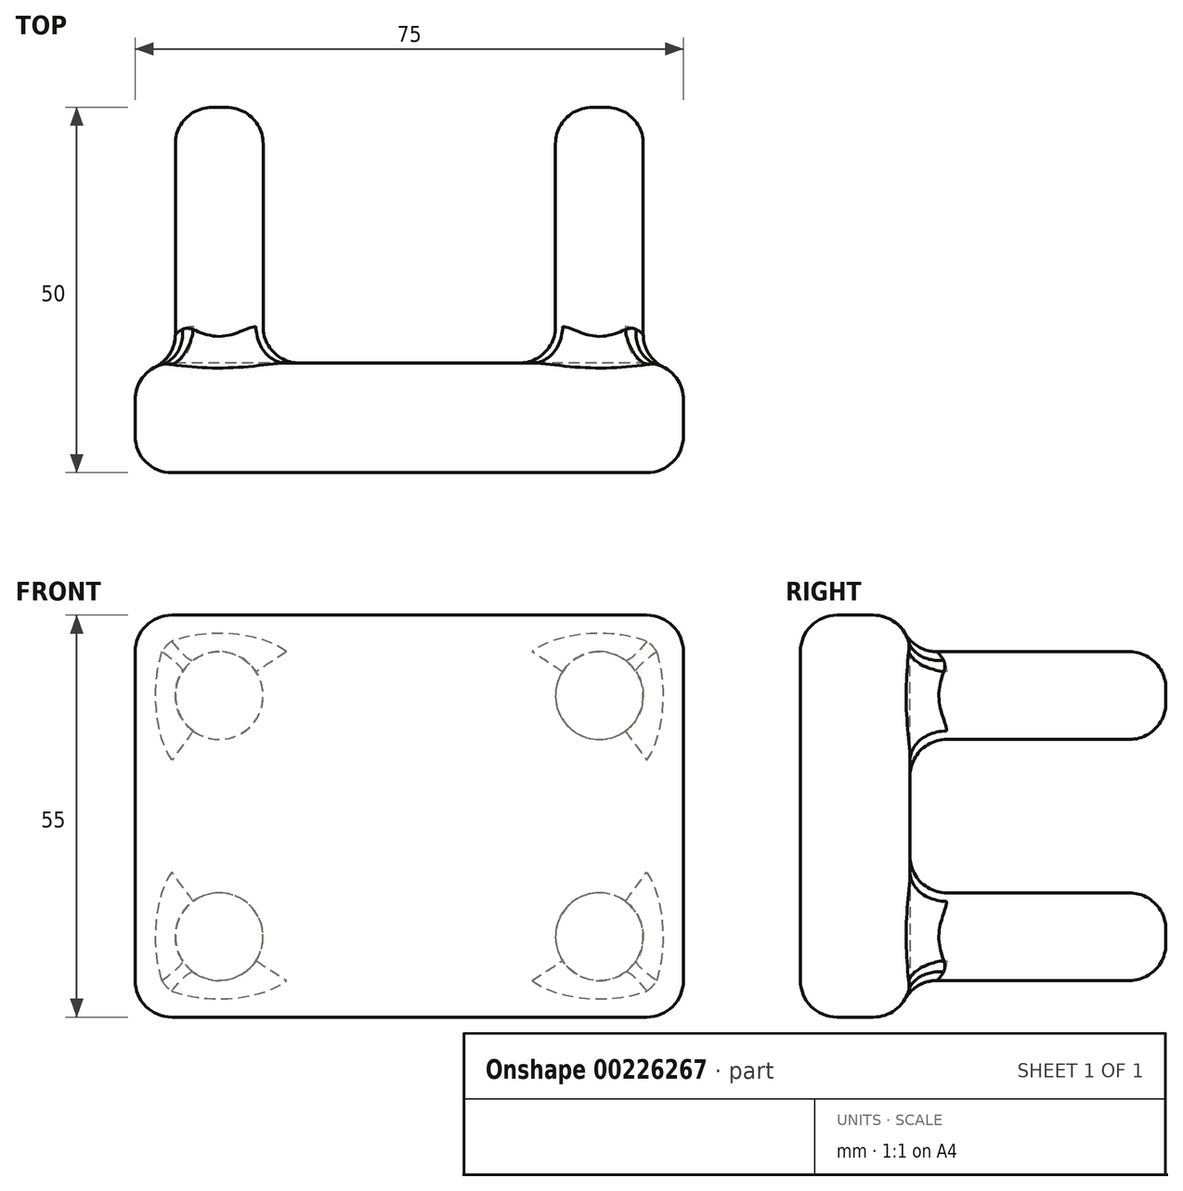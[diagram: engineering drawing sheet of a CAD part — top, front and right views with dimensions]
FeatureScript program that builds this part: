
annotation { "Feature Type Name" : "Feature", "Feature Type Description" : "" }
export const myFeature = defineFeature(function(context is Context, id is Id, definition is map)
    precondition{}
    {
        {
            var Q0;
            Q0=qCreatedBy(makeId("Front.planeOp"),FACE);
            var sketch = newSketch(context, id + "F0", { "sketchPlane" : qUnion([Q0])});
            skLineSegment(sketch, "E0.bottom", {"start": v(37.5, -27.5) * mm, "end": v(-37.5, -27.5) * mm});
            skLineSegment(sketch, "E0.top", {"start": v(37.5, 27.5) * mm, "end": v(-37.5, 27.5) * mm});
            skLineSegment(sketch, "E0.left", {"start": v(37.5, -27.5) * mm, "end": v(37.5, 27.5) * mm});
            skLineSegment(sketch, "E0.right", {"start": v(-37.5, -27.5) * mm, "end": v(-37.5, 27.5) * mm});
            skPoint(sketch, "E0.middle", {"position": v(0, 0) * mm});
            skSolve(sketch);
        }
        {
            var Q0;
            Q0 = qSketchRegion(id + "F0", true);
            extrude(context, id + "F1", {"entities" : qUnion([Q0]), "depth" : 15 * mm});
        }
        {
            var Q0;
            Q0=makeQuery(id+"F1.opExtrude","CAP_FACE",FACE,{"disambiguationData":[OSD([sQuery(id+"F0.wireOp",EDGE,"E0.bottom"),sQuery(id+"F0.wireOp",EDGE,"E0.top"),sQuery(id+"F0.wireOp",EDGE,"E0.left"),sQuery(id+"F0.wireOp",EDGE,"E0.right")])],"isStart":true});
            var sketch = newSketch(context, id + "F2", { "sketchPlane" : qUnion([Q0])});
            skCircle(sketch, "E1", {"center": v(-26, 16.5) * mm, "radius": 6 * mm});
            skCircle(sketch, "E2.MirrorC", {"center": v(26, 16.5) * mm, "radius": 6 * mm});
            skCircle(sketch, "E3.MirrorC", {"center": v(26, -16.5) * mm, "radius": 6 * mm});
            skCircle(sketch, "E4.MirrorC", {"center": v(-26, -16.5) * mm, "radius": 6 * mm});
            skSolve(sketch);
        }
        {
            var Q0;
            Q0 = qSketchRegion(id + "F2", true);
            extrude(context, id + "F3", {"entities" : qUnion([Q0]), "operationType" : NewBodyOperationType.ADD, "depth" : 35 * mm});
        }
        {
            var Q0;
            Q0=makeQuery(id+"F1.opExtrude","SWEPT_FACE",FACE,{"disambiguationData":[OSD([sQuery(id+"F0.wireOp",EDGE,"E0.top")])]});
            var Q1;
            Q1=makeQuery(id+"F1.opExtrude","CAP_FACE",FACE,{"disambiguationData":[OSD([sQuery(id+"F0.wireOp",EDGE,"E0.bottom"),sQuery(id+"F0.wireOp",EDGE,"E0.top"),sQuery(id+"F0.wireOp",EDGE,"E0.left"),sQuery(id+"F0.wireOp",EDGE,"E0.right")])],"isStart":false});
            var Q2;
            Q2=makeQuery(id+"F1.opExtrude","SWEPT_FACE",FACE,{"disambiguationData":[OSD([sQuery(id+"F0.wireOp",EDGE,"E0.right")])]});
            var Q3;
            Q3=makeQuery(id+"F1.opExtrude","SWEPT_FACE",FACE,{"disambiguationData":[OSD([sQuery(id+"F0.wireOp",EDGE,"E0.bottom")])]});
            var Q4;
            Q4=makeQuery(id+"F1.opExtrude","SWEPT_FACE",FACE,{"disambiguationData":[OSD([sQuery(id+"F0.wireOp",EDGE,"E0.left")])]});
            fillet(context, id + "F4", {"entities" : qUnion([Q0, Q1, Q2, Q3, Q4]), "radius" : 5 * mm, "tangentPropagation" : true, "allowEdgeOverflow" : false});
        }
        {
            var Q0;
            {var subQ0=sQuery(id+"F0.wireOp",EDGE,"E0.right");var subQ1=sQuery(id+"F0.wireOp",EDGE,"E0.bottom");Q0=makeQuery(id+"F4.opFillet","BLEND_FACE",FACE,{"disambiguationData":[OSD([subQ1,subQ0]),TDD([makeQuery(id+"F1.opExtrude","CAP_VERTEX",VERTEX,{"disambiguationData":[OSD([subQ1,subQ0])],"isStart":true})])]});}
            var Q1;
            {var subQ0=sQuery(id+"F0.wireOp",EDGE,"E0.right");Q1=makeQuery(id+"F4.opFillet","BLEND_FACE",FACE,{"disambiguationData":[OSD([subQ0]),TDD([makeQuery(id+"F1.opExtrude","CAP_EDGE",EDGE,{"disambiguationData":[OSD([subQ0])],"isStart":true})])]});}
            var Q2;
            {var subQ0=sQuery(id+"F0.wireOp",EDGE,"E0.right");Q2=makeQuery(id+"F4.opFillet","BLEND_EDGE",EDGE,{"blendedFrom":[makeQuery(id+"F1.opExtrude","CAP_VERTEX",VERTEX,{"disambiguationData":[OSD([sQuery(id+"F0.wireOp",EDGE,"E0.bottom"),subQ0])],"isStart":true}),makeQuery(id+"F1.opExtrude","CAP_EDGE",EDGE,{"disambiguationData":[OSD([subQ0])],"isStart":true})],"blendedInto":[]});}
            var Q3;
            Q3=makeQuery(id+"F3.opExtrude","SWEPT_FACE",FACE,{"disambiguationData":[OSD([sQuery(id+"F2.wireOp",EDGE,"E2.MirrorC")])]});
            var Q4;
            Q4=makeQuery(id+"F3.opExtrude","SWEPT_FACE",FACE,{"disambiguationData":[OSD([sQuery(id+"F2.wireOp",EDGE,"E1")])]});
            var Q5;
            Q5=makeQuery(id+"F3.opExtrude","SWEPT_FACE",FACE,{"disambiguationData":[OSD([sQuery(id+"F2.wireOp",EDGE,"E3.MirrorC")])]});
            var Q6;
            Q6=makeQuery(id+"F3.opExtrude","SWEPT_FACE",FACE,{"disambiguationData":[OSD([sQuery(id+"F2.wireOp",EDGE,"E4.MirrorC")])]});
            fillet(context, id + "F5", {"entities" : qUnion([Q0, Q1, Q2, Q3, Q4, Q5, Q6]), "radius" : 5 * mm, "tangentPropagation" : true, "allowEdgeOverflow" : false});
        }
    });
